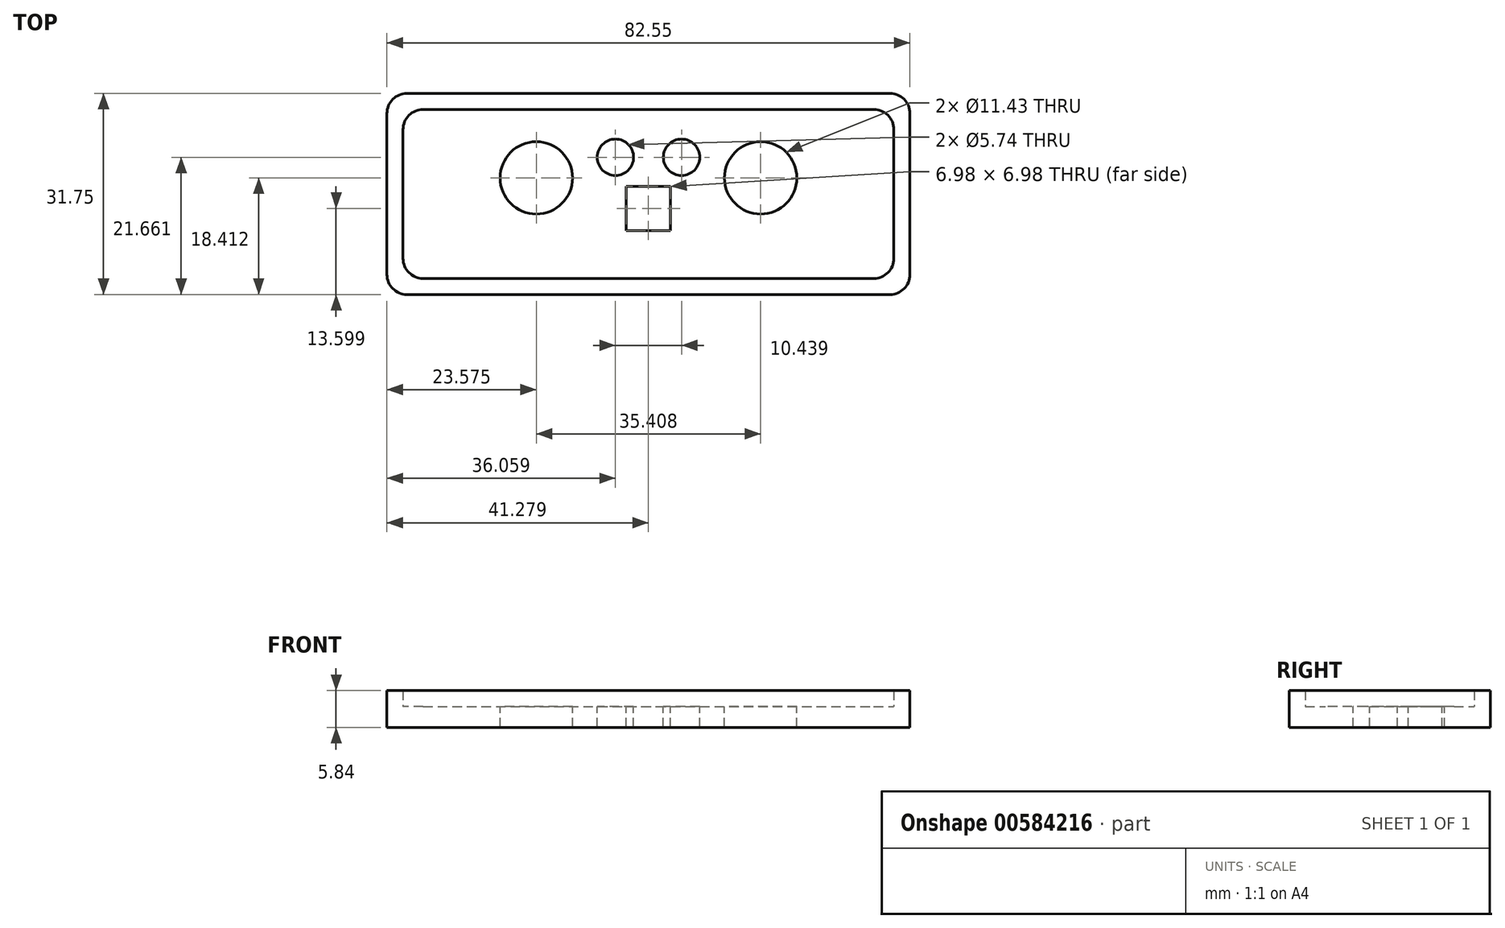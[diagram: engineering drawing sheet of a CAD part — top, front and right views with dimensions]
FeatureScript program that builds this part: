
annotation { "Feature Type Name" : "Feature", "Feature Type Description" : "" }
export const myFeature = defineFeature(function(context is Context, id is Id, definition is map)
    precondition{}
    {
        {
            var Q0;
            Q0=qCreatedBy(makeId("Top.planeOp"),FACE);
            var sketch = newSketch(context, id + "F0", { "sketchPlane" : qUnion([Q0])});
            skLineSegment(sketch, "E0.bottom", {"start": v(12.86, -33.07) * mm, "end": v(83.98, -33.07) * mm});
            skLineSegment(sketch, "E0.top", {"start": v(12.86, -6.4) * mm, "end": v(83.98, -6.4) * mm});
            skLineSegment(sketch, "E0.left", {"start": v(9.68, -9.58) * mm, "end": v(9.68, -29.9) * mm});
            skLineSegment(sketch, "E0.right", {"start": v(87.15, -9.58) * mm, "end": v(87.15, -29.9) * mm});
            skPoint(sketch, "E1", {"position": v(48.42, -6.4) * mm});
            skPoint(sketch, "E2", {"position": v(9.68, -19.74) * mm});
            skLineSegment(sketch, "E3.0", {"start": v(10.32, -3.86) * mm, "end": v(86.52, -3.86) * mm});
            skLineSegment(sketch, "E3.1", {"start": v(7.14, -7.04) * mm, "end": v(7.14, -32.44) * mm});
            skLineSegment(sketch, "E3.2", {"start": v(10.32, -35.61) * mm, "end": v(86.52, -35.61) * mm});
            skLineSegment(sketch, "E3.3", {"start": v(89.7, -7.04) * mm, "end": v(89.7, -32.44) * mm});
            skPoint(sketch, "E4.visualSharp", {"position": v(87.15, -33.07) * mm});
            skArc(sketch, "E4.filletArc", {"start": v(83.98, -33.07) * mm, "mid": v(86.22, -32.14) * mm, "end": v(87.15, -29.9) * mm});
            skPoint(sketch, "E5.visualSharp", {"position": v(87.15, -6.4) * mm});
            skArc(sketch, "E5.filletArc", {"start": v(87.15, -9.58) * mm, "mid": v(86.22, -7.33) * mm, "end": v(83.98, -6.4) * mm});
            skPoint(sketch, "E6.visualSharp", {"position": v(89.7, -35.61) * mm});
            skArc(sketch, "E6.filletArc", {"start": v(86.52, -35.61) * mm, "mid": v(88.76, -34.68) * mm, "end": v(89.7, -32.44) * mm});
            skPoint(sketch, "E7.visualSharp", {"position": v(89.7, -3.86) * mm});
            skArc(sketch, "E7.filletArc", {"start": v(89.7, -7.04) * mm, "mid": v(88.76, -4.8) * mm, "end": v(86.52, -3.86) * mm});
            skPoint(sketch, "E8.visualSharp", {"position": v(9.68, -33.07) * mm});
            skArc(sketch, "E8.filletArc", {"start": v(9.68, -29.9) * mm, "mid": v(10.61, -32.14) * mm, "end": v(12.86, -33.07) * mm});
            skPoint(sketch, "E9.visualSharp", {"position": v(7.14, -35.61) * mm});
            skArc(sketch, "E9.filletArc", {"start": v(7.14, -32.44) * mm, "mid": v(8.07, -34.68) * mm, "end": v(10.32, -35.61) * mm});
            skPoint(sketch, "E10.visualSharp", {"position": v(7.14, -3.86) * mm});
            skArc(sketch, "E10.filletArc", {"start": v(10.32, -3.86) * mm, "mid": v(8.07, -4.8) * mm, "end": v(7.14, -7.04) * mm});
            skPoint(sketch, "E11.visualSharp", {"position": v(9.68, -6.4) * mm});
            skArc(sketch, "E11.filletArc", {"start": v(12.86, -6.4) * mm, "mid": v(10.61, -7.33) * mm, "end": v(9.68, -9.58) * mm});
            skSolve(sketch);
        }
        {
            var Q0;
            Q0=makeQuery(id+"F0.imprint","IMPRINT",FACE,{"disambiguationData":[TD([[makeQuery(id+"F0.imprint","IMPRINT",EDGE,{"derivedFrom":sQuery(id+"F0.wireOp",EDGE,"E0.bottom")}),-1.0]])]});
            var Q1;
            Q1=makeQuery(id+"F0.imprint","IMPRINT",FACE,{"disambiguationData":[TD([[makeQuery(id+"F0.imprint","IMPRINT",EDGE,{"derivedFrom":sQuery(id+"F0.wireOp",EDGE,"E0.bottom")}),1.0]])]});
            extrude(context, id + "F1", {"entities" : qUnion([Q0, Q1]), "oppositeDirection" : true, "depth" : 3.3 * mm, "offsetDistance" : 25.4 * mm});
        }
        {
            var Q0;
            Q0=makeQuery(id+"F0.imprint","IMPRINT",FACE,{"disambiguationData":[TD([[makeQuery(id+"F0.imprint","IMPRINT",EDGE,{"derivedFrom":sQuery(id+"F0.wireOp",EDGE,"E0.bottom")}),-1.0]])]});
            extrude(context, id + "F2", {"entities" : qUnion([Q0]), "operationType" : NewBodyOperationType.ADD, "depth" : 2.54 * mm, "offsetDistance" : 25.4 * mm});
        }
        {
            var Q0;
            Q0=qCreatedBy(makeId("Top.planeOp"),FACE);
            var sketch = newSketch(context, id + "F3", { "sketchPlane" : qUnion([Q0])});
            skCircle(sketch, "E12", {"center": v(30.72, -17.2) * mm, "radius": 5.72 * mm});
            skCircle(sketch, "E13", {"center": v(66.12, -17.2) * mm, "radius": 5.72 * mm});
            skLineSegment(sketch, "E14.bottom", {"start": v(44.93, -18.52) * mm, "end": v(51.91, -18.52) * mm});
            skLineSegment(sketch, "E14.top", {"start": v(44.93, -25.5) * mm, "end": v(51.91, -25.5) * mm});
            skLineSegment(sketch, "E14.left", {"start": v(44.93, -18.52) * mm, "end": v(44.93, -25.5) * mm});
            skLineSegment(sketch, "E14.right", {"start": v(51.91, -18.52) * mm, "end": v(51.91, -25.5) * mm});
            skPoint(sketch, "E15", {"position": v(48.42, -18.52) * mm});
            skCircle(sketch, "E16", {"center": v(43.2, -13.95) * mm, "radius": 2.87 * mm});
            skCircle(sketch, "E17", {"center": v(53.64, -13.95) * mm, "radius": 2.87 * mm});
            skLineSegment(sketch, "E18", {"start": v(43.2, -13.95) * mm, "end": v(53.64, -13.95) * mm});
            skPoint(sketch, "E19", {"position": v(48.42, -13.95) * mm});
            skLineSegment(sketch, "E20", {"start": v(30.72, -17.2) * mm, "end": v(66.12, -17.2) * mm});
            skPoint(sketch, "E21", {"position": v(48.42, -17.2) * mm});
            skSolve(sketch);
        }
        {
            var Q0;
            Q0=qSketchRegion(id+"F3",true);
            extrude(context, id + "F4", {"entities" : qUnion([Q0]), "operationType" : NewBodyOperationType.REMOVE, "endBound" : BoundingType.THROUGH_ALL, "oppositeDirection" : true, "depth" : 25.4 * mm, "offsetDistance" : 25.4 * mm});
        }
    });
